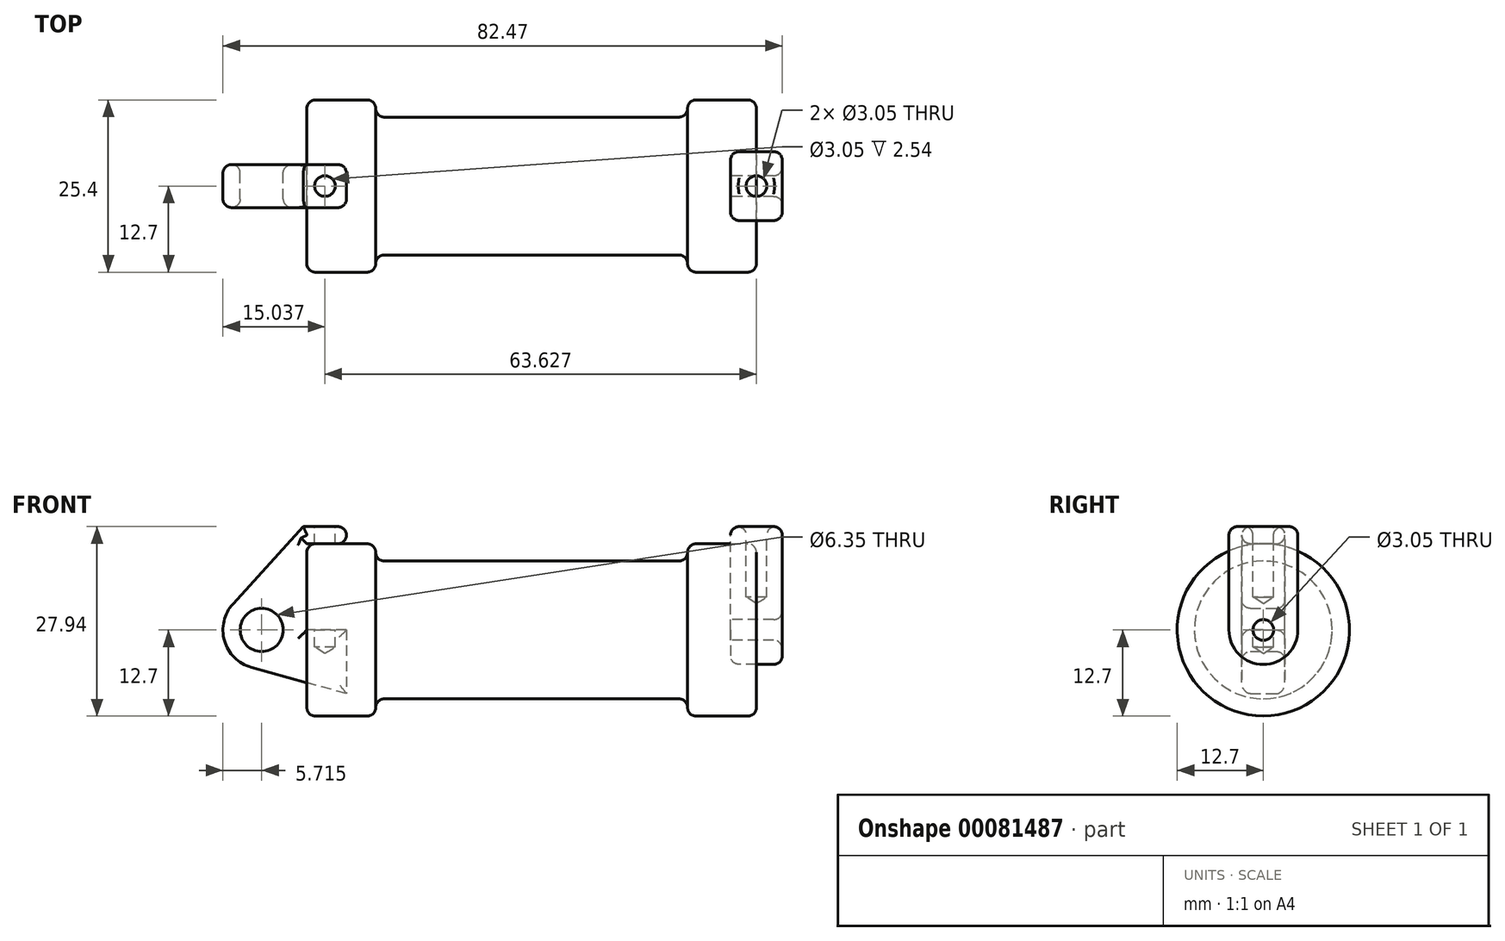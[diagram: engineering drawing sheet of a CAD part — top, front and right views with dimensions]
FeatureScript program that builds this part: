
annotation { "Feature Type Name" : "Feature", "Feature Type Description" : "" }
export const myFeature = defineFeature(function(context is Context, id is Id, definition is map)
    precondition{}
    {
        {
            var Q0;
            Q0=qCreatedBy(makeId("Front.planeOp"),FACE);
            var sketch = newSketch(context, id + "F0", { "sketchPlane" : qUnion([Q0])});
            skLineSegment(sketch, "E0", {"start": v(0, 0) * mm, "end": v(0, 12.7) * mm});
            skLineSegment(sketch, "E1", {"start": v(0, 12.7) * mm, "end": v(10.16, 12.7) * mm});
            skLineSegment(sketch, "E2", {"start": v(10.16, 12.7) * mm, "end": v(10.16, 10.16) * mm});
            skLineSegment(sketch, "E3", {"start": v(10.16, 10.16) * mm, "end": v(56.13, 10.16) * mm});
            skLineSegment(sketch, "E4", {"start": v(56.13, 10.16) * mm, "end": v(56.13, 12.7) * mm});
            skLineSegment(sketch, "E5", {"start": v(56.13, 12.7) * mm, "end": v(66.3, 12.7) * mm});
            skLineSegment(sketch, "E6", {"start": v(66.3, 12.7) * mm, "end": v(66.3, 0) * mm});
            skLineSegment(sketch, "E7", {"start": v(66.3, 0) * mm, "end": v(0, 0) * mm});
            skLineSegment(sketch, "E8", {"start": v(5.84, 15.24) * mm, "end": v(-0.5, 15.24) * mm});
            skLineSegment(sketch, "E9", {"start": v(-0.5, 15.24) * mm, "end": v(-10.88, 3.85) * mm});
            skLineSegment(sketch, "E10", {"start": v(0, 0) * mm, "end": v(-6.65, 0) * mm});
            skCircle(sketch, "E11", {"center": v(-6.65, 0) * mm, "radius": 5.72 * mm});
            skCircle(sketch, "E12", {"center": v(-6.65, 0) * mm, "radius": 3.18 * mm});
            skLineSegment(sketch, "E13", {"start": v(5.84, 15.24) * mm, "end": v(5.84, -9.4) * mm});
            skLineSegment(sketch, "E14", {"start": v(5.84, -9.4) * mm, "end": v(-8.18, -5.5) * mm});
            skSolve(sketch);
        }
        {
            var Q0;
            {var subQ0=sQuery(id+"F0.wireOp",EDGE,"E2");Q0=makeQuery(id+"F0.imprint","IMPRINT",FACE,{"disambiguationData":[TD([[makeQuery(id+"F0.imprint","IMPRINT",EDGE,{"derivedFrom":subQ0}),-1.0]])]});}
            var Q1;
            {var subQ0=sQuery(id+"F0.wireOp",EDGE,"E0");Q1=makeQuery(id+"F0.imprint","IMPRINT",FACE,{"disambiguationData":[TD([[makeQuery(id+"F0.imprint","IMPRINT",EDGE,{"derivedFrom":subQ0}),-1.0]])]});}
            var Q2;
            Q2=sQuery(id+"F0.wireOp",EDGE,"E7");
            revolve(context, id + "F1", {"entities" : qUnion([Q0, Q1]), "axis" : qUnion([Q2]), "revolveType" : RevolveType.FULL});
        }
        {
            var Q0;
            {var subQ3=sQuery(id+"F0.wireOp",EDGE,"E0");Q0=makeQuery(id+"F0.imprint","IMPRINT",FACE,{"disambiguationData":[TD([[makeQuery(id+"F0.imprint","IMPRINT",EDGE,{"derivedFrom":subQ3}),1.0]])]});}
            var Q1;
            {var subQ4=sQuery(id+"F0.wireOp",EDGE,"E12");Q1=makeQuery(id+"F0.imprint","IMPRINT",FACE,{"disambiguationData":[TD([[makeQuery(id+"F0.imprint","IMPRINT",EDGE,{"derivedFrom":subQ4}),-1.0]])]});}
            var Q2;
            {var subQ0=sQuery(id+"F0.wireOp",EDGE,"E14");Q2=makeQuery(id+"F0.imprint","IMPRINT",FACE,{"disambiguationData":[TD([[makeQuery(id+"F0.imprint","IMPRINT",EDGE,{"derivedFrom":subQ0}),-1.0]])]});}
            extrude(context, id + "F2", {"entities" : qUnion([Q0, Q1, Q2]), "endBound" : BoundingType.SYMMETRIC, "depth" : 6.35 * mm});
        }
        {
            var Q0;
            Q0=makeQuery(id+"F1.opRevolve","SWEPT_FACE",FACE,{"disambiguationData":[OSD([sQuery(id+"F0.wireOp",EDGE,"E6")])]});
            var sketch = newSketch(context, id + "F3", { "sketchPlane" : qUnion([Q0])});
            skCircle(sketch, "E15", {"center": v(0, 0) * mm, "radius": 5.08 * mm});
            skCircle(sketch, "E16", {"center": v(0, 0) * mm, "radius": 1.52 * mm});
            skLineSegment(sketch, "E17", {"start": v(-5.08, 0) * mm, "end": v(-5.08, 15.24) * mm});
            skLineSegment(sketch, "E18", {"start": v(5.08, 0) * mm, "end": v(5.08, 15.24) * mm});
            skLineSegment(sketch, "E19", {"start": v(-5.08, 15.24) * mm, "end": v(5.08, 15.24) * mm});
            skSolve(sketch);
        }
        {
            var Q0;
            {var subQ0=sQuery(id+"F3.wireOp",EDGE,"E17");var subQ1=sQuery(id+"F3.wireOp",EDGE,"E15");var subQ2=makeQuery(id+"F3.imprint","INTERSECT",VERTEX,{"derivedFrom":[subQ1,subQ0]});Q0=makeQuery(id+"F3.imprint","IMPRINT",FACE,{"disambiguationData":[TD([[makeQuery(id+"F3.imprint","IMPRINT",EDGE,{"disambiguationData":[TD([[subQ2,1.0]])],"derivedFrom":subQ1}),-1.0]])]});}
            var Q1;
            {var subQ0=sQuery(id+"F3.wireOp",EDGE,"E19");Q1=makeQuery(id+"F3.imprint","IMPRINT",FACE,{"disambiguationData":[TD([[makeQuery(id+"F3.imprint","IMPRINT",EDGE,{"derivedFrom":subQ0}),-1.0]])]});}
            var Q2;
            Q2=makeQuery(id+"F3.imprint","IMPRINT",FACE,{"disambiguationData":[TD([[makeQuery(id+"F3.imprint","IMPRINT",EDGE,{"derivedFrom":sQuery(id+"F3.wireOp",EDGE,"E16")}),-1.0]])]});
            extrude(context, id + "F4", {"entities" : qUnion([Q0, Q1, Q2]), "endBound" : BoundingType.SYMMETRIC, "depth" : 7.62 * mm});
        }
        {
            var Q0;
            Q0=makeQuery(id+"F2.opExtrude","SWEPT_FACE",FACE,{"disambiguationData":[OSD([sQuery(id+"F0.wireOp",EDGE,"E8")])]});
            var sketch = newSketch(context, id + "F5", { "sketchPlane" : qUnion([Q0])});
            skCircle(sketch, "E20", {"center": v(2.67, 0) * mm, "radius": 1.52 * mm});
            skSolve(sketch);
        }
        {
            var Q0;
            Q0=makeQuery(id+"F4.opExtrude","SWEPT_FACE",FACE,{"disambiguationData":[OSD([sQuery(id+"F3.wireOp",EDGE,"E19")])]});
            var sketch = newSketch(context, id + "F6", { "sketchPlane" : qUnion([Q0])});
            skCircle(sketch, "E21", {"center": v(66.3, 0) * mm, "radius": 1.52 * mm});
            skSolve(sketch);
        }
        {
            var Q0;
            Q0=sQuery(id+"F5.wireOp",VERTEX,"E20.center");
            var Q1;
            Q1=makeQuery(id+"F2.opExtrude","SWEPT_BODY",BODY,{"disambiguationData":[OSD([sQuery(id+"F0.wireOp",EDGE,"E0"),sQuery(id+"F0.wireOp",EDGE,"E1"),sQuery(id+"F0.wireOp",EDGE,"E7"),sQuery(id+"F0.wireOp",EDGE,"E8"),sQuery(id+"F0.wireOp",EDGE,"E9"),sQuery(id+"F0.wireOp",EDGE,"E11"),sQuery(id+"F0.wireOp",EDGE,"E12"),sQuery(id+"F0.wireOp",EDGE,"E13"),sQuery(id+"F0.wireOp",EDGE,"E14")])]});
            hole(context, id + "F7", {"style" : HoleStyle.SIMPLE, "endStyle" : HoleEndStyle.BLIND, "holeDiameter" : 3.05 * mm, "holeDepth" : 17.78 * mm, "locations" : qUnion([Q0]), "scope" : qUnion([Q1])});
        }
        {
            var Q0;
            Q0=sQuery(id+"F6.wireOp",VERTEX,"E21.center");
            var Q1;
            Q1=makeQuery(id+"F4.opExtrude","SWEPT_BODY",BODY,{"disambiguationData":[OSD([sQuery(id+"F3.wireOp",EDGE,"E15"),sQuery(id+"F3.wireOp",EDGE,"E16"),sQuery(id+"F3.wireOp",EDGE,"E17"),sQuery(id+"F3.wireOp",EDGE,"E18"),sQuery(id+"F3.wireOp",EDGE,"E19")])]});
            hole(context, id + "F8", {"style" : HoleStyle.SIMPLE, "endStyle" : HoleEndStyle.BLIND, "holeDiameter" : 3.05 * mm, "holeDepth" : 10.4 * mm, "locations" : qUnion([Q0]), "scope" : qUnion([Q1])});
        }
        {
            var Q0;
            Q0=makeQuery(id+"F1.opRevolve","SWEPT_EDGE",EDGE,{"disambiguationData":[OSD([sQuery(id+"F0.wireOp",EDGE,"E1"),sQuery(id+"F0.wireOp",EDGE,"E2")])]});
            var Q1;
            Q1=makeQuery(id+"F1.opRevolve","SWEPT_EDGE",EDGE,{"disambiguationData":[OSD([sQuery(id+"F0.wireOp",EDGE,"E2"),sQuery(id+"F0.wireOp",EDGE,"E3")])]});
            var Q2;
            Q2=makeQuery(id+"F1.opRevolve","SWEPT_EDGE",EDGE,{"disambiguationData":[OSD([sQuery(id+"F0.wireOp",EDGE,"E4"),sQuery(id+"F0.wireOp",EDGE,"E5")])]});
            var Q3;
            Q3=makeQuery(id+"F1.opRevolve","SWEPT_EDGE",EDGE,{"disambiguationData":[OSD([sQuery(id+"F0.wireOp",EDGE,"E3"),sQuery(id+"F0.wireOp",EDGE,"E4")])]});
            var Q4;
            Q4=makeQuery(id+"F1.opRevolve","SWEPT_FACE",FACE,{"disambiguationData":[OSD([sQuery(id+"F0.wireOp",EDGE,"E4")])]});
            var Q5;
            Q5=makeQuery(id+"F1.opRevolve","SWEPT_FACE",FACE,{"disambiguationData":[OSD([sQuery(id+"F0.wireOp",EDGE,"E3")])]});
            var Q6;
            Q6=makeQuery(id+"F1.opRevolve","SWEPT_EDGE",EDGE,{"disambiguationData":[OSD([sQuery(id+"F0.wireOp",EDGE,"E5"),sQuery(id+"F0.wireOp",EDGE,"E6")])]});
            var Q7;
            Q7=makeQuery(id+"F1.opRevolve","SWEPT_EDGE",EDGE,{"disambiguationData":[OSD([sQuery(id+"F0.wireOp",EDGE,"E0"),sQuery(id+"F0.wireOp",EDGE,"E1")])]});
            fillet(context, id + "F9", {"entities" : qUnion([Q0, Q1, Q2, Q3, Q4, Q5, Q6, Q7]), "radius" : 1.27 * mm, "tangentPropagation" : true, "allowEdgeOverflow" : false});
        }
        {
            var Q0;
            {var subQ0=sQuery(id+"F0.wireOp",EDGE,"E13");Q0=makeQuery(id+"F2.opExtrude","CAP_EDGE",EDGE,{"disambiguationData":[OSD([subQ0]),TDD([makeQuery(id+"F0.imprint","IMPRINT",EDGE,{"disambiguationData":[TD([[makeQuery(id+"F0.imprint","INTERSECT",VERTEX,{"derivedFrom":[sQuery(id+"F0.wireOp",EDGE,"E8"),subQ0]}),-1.0]])],"derivedFrom":subQ0})])],"isStart":false});}
            var Q1;
            Q1=makeQuery(id+"F2.opExtrude","SWEPT_EDGE",EDGE,{"disambiguationData":[OSD([sQuery(id+"F0.wireOp",EDGE,"E8"),sQuery(id+"F0.wireOp",EDGE,"E13")])]});
            var Q2;
            {var subQ0=sQuery(id+"F0.wireOp",EDGE,"E13");Q2=makeQuery(id+"F2.opExtrude","CAP_EDGE",EDGE,{"disambiguationData":[OSD([subQ0]),TDD([makeQuery(id+"F0.imprint","IMPRINT",EDGE,{"disambiguationData":[TD([[makeQuery(id+"F0.imprint","INTERSECT",VERTEX,{"derivedFrom":[sQuery(id+"F0.wireOp",EDGE,"E8"),subQ0]}),-1.0]])],"derivedFrom":subQ0})])],"isStart":true});}
            var Q3;
            Q3=makeQuery(id+"F2.opExtrude","SWEPT_EDGE",EDGE,{"disambiguationData":[OSD([sQuery(id+"F0.wireOp",EDGE,"E1"),sQuery(id+"F0.wireOp",EDGE,"E13")])]});
            var Q4;
            Q4=makeQuery(id+"F2.opExtrude","CAP_FACE",FACE,{"disambiguationData":[OSD([sQuery(id+"F0.wireOp",EDGE,"E0"),sQuery(id+"F0.wireOp",EDGE,"E1"),sQuery(id+"F0.wireOp",EDGE,"E7"),sQuery(id+"F0.wireOp",EDGE,"E8"),sQuery(id+"F0.wireOp",EDGE,"E9"),sQuery(id+"F0.wireOp",EDGE,"E11"),sQuery(id+"F0.wireOp",EDGE,"E12"),sQuery(id+"F0.wireOp",EDGE,"E13"),sQuery(id+"F0.wireOp",EDGE,"E14")])],"isStart":false});
            var Q5;
            Q5=makeQuery(id+"F2.opExtrude","CAP_FACE",FACE,{"disambiguationData":[OSD([sQuery(id+"F0.wireOp",EDGE,"E0"),sQuery(id+"F0.wireOp",EDGE,"E1"),sQuery(id+"F0.wireOp",EDGE,"E7"),sQuery(id+"F0.wireOp",EDGE,"E8"),sQuery(id+"F0.wireOp",EDGE,"E9"),sQuery(id+"F0.wireOp",EDGE,"E11"),sQuery(id+"F0.wireOp",EDGE,"E12"),sQuery(id+"F0.wireOp",EDGE,"E13"),sQuery(id+"F0.wireOp",EDGE,"E14")])],"isStart":true});
            var Q6;
            Q6=makeQuery(id+"F4.opExtrude","SWEPT_FACE",FACE,{"disambiguationData":[OSD([sQuery(id+"F3.wireOp",EDGE,"E18")])]});
            var Q7;
            Q7=makeQuery(id+"F4.opExtrude","SWEPT_FACE",FACE,{"disambiguationData":[OSD([sQuery(id+"F3.wireOp",EDGE,"E15")])]});
            var Q8;
            Q8=makeQuery(id+"F4.opExtrude","SWEPT_FACE",FACE,{"disambiguationData":[OSD([sQuery(id+"F3.wireOp",EDGE,"E19")])]});
            var Q9;
            Q9=makeQuery(id+"F4.opExtrude","CAP_FACE",FACE,{"disambiguationData":[OSD([sQuery(id+"F3.wireOp",EDGE,"E15"),sQuery(id+"F3.wireOp",EDGE,"E16"),sQuery(id+"F3.wireOp",EDGE,"E17"),sQuery(id+"F3.wireOp",EDGE,"E18"),sQuery(id+"F3.wireOp",EDGE,"E19")])],"isStart":false});
            fillet(context, id + "F10", {"entities" : qUnion([Q0, Q1, Q2, Q3, Q4, Q5, Q6, Q7, Q8, Q9]), "radius" : 1.27 * mm, "tangentPropagation" : true, "allowEdgeOverflow" : false});
        }
        {
            var Q0;
            Q0=makeQuery(id+"F1.opRevolve","SWEPT_FACE",FACE,{"disambiguationData":[OSD([sQuery(id+"F0.wireOp",EDGE,"E6")])]});
            var Q1;
            Q1=makeQuery(id+"F4.opExtrude","SWEPT_FACE",FACE,{"disambiguationData":[OSD([sQuery(id+"F3.wireOp",EDGE,"E18")])]});
            var Q2;
            {var subQ0=sQuery(id+"F3.wireOp",EDGE,"E18");Q2=makeQuery(id+"F10.opFillet","BLEND_EDGE",EDGE,{"blendedFrom":[makeQuery(id+"F4.opExtrude","CAP_EDGE",EDGE,{"disambiguationData":[OSD([subQ0])],"isStart":true}),makeQuery(id+"F4.opExtrude","SWEPT_FACE",FACE,{"disambiguationData":[OSD([subQ0])]})],"blendedInto":[makeQuery(id+"F4.opExtrude","SWEPT_FACE",FACE,{"disambiguationData":[OSD([subQ0])]})]});}
            var Q3;
            {var subQ0=sQuery(id+"F3.wireOp",EDGE,"E18");Q3=makeQuery(id+"F10.opFillet","BLEND_FACE",FACE,{"disambiguationData":[OSD([subQ0]),TDD([makeQuery(id+"F4.opExtrude","CAP_EDGE",EDGE,{"disambiguationData":[OSD([subQ0])],"isStart":false})])]});}
            var Q4;
            Q4=makeQuery(id+"F4.opExtrude","CAP_FACE",FACE,{"disambiguationData":[OSD([sQuery(id+"F3.wireOp",EDGE,"E15"),sQuery(id+"F3.wireOp",EDGE,"E16"),sQuery(id+"F3.wireOp",EDGE,"E17"),sQuery(id+"F3.wireOp",EDGE,"E18"),sQuery(id+"F3.wireOp",EDGE,"E19")])],"isStart":false});
            var Q5;
            {var subQ0=sQuery(id+"F3.wireOp",EDGE,"E17");Q5=makeQuery(id+"F10.opFillet","BLEND_EDGE",EDGE,{"blendedFrom":[makeQuery(id+"F4.opExtrude","CAP_EDGE",EDGE,{"disambiguationData":[OSD([subQ0])],"isStart":false}),makeQuery(id+"F4.opExtrude","SWEPT_FACE",FACE,{"disambiguationData":[OSD([subQ0])]})],"blendedInto":[makeQuery(id+"F4.opExtrude","SWEPT_FACE",FACE,{"disambiguationData":[OSD([subQ0])]})]});}
            var Q6;
            {var subQ0=sQuery(id+"F3.wireOp",EDGE,"E17");Q6=makeQuery(id+"F10.opFillet","BLEND_FACE",FACE,{"disambiguationData":[OSD([subQ0]),TDD([makeQuery(id+"F4.opExtrude","CAP_EDGE",EDGE,{"disambiguationData":[OSD([subQ0])],"isStart":false})])]});}
            var Q7;
            Q7=makeQuery(id+"F4.opExtrude","SWEPT_FACE",FACE,{"disambiguationData":[OSD([sQuery(id+"F3.wireOp",EDGE,"E17")])]});
            var Q8;
            Q8=makeQuery(id+"F4.opExtrude","CAP_FACE",FACE,{"disambiguationData":[OSD([sQuery(id+"F3.wireOp",EDGE,"E15"),sQuery(id+"F3.wireOp",EDGE,"E16"),sQuery(id+"F3.wireOp",EDGE,"E17"),sQuery(id+"F3.wireOp",EDGE,"E18"),sQuery(id+"F3.wireOp",EDGE,"E19")])],"isStart":true});
            var Q9;
            {var subQ0=sQuery(id+"F3.wireOp",EDGE,"E19");Q9=makeQuery(id+"F10.opFillet","BLEND_EDGE",EDGE,{"blendedFrom":[makeQuery(id+"F4.opExtrude","CAP_VERTEX",VERTEX,{"disambiguationData":[OSD([sQuery(id+"F3.wireOp",EDGE,"E18"),subQ0])],"isStart":true}),makeQuery(id+"F4.opExtrude","CAP_EDGE",EDGE,{"disambiguationData":[OSD([subQ0])],"isStart":true})],"blendedInto":[]});}
            var Q10;
            {var subQ0=sQuery(id+"F3.wireOp",EDGE,"E18");Q10=makeQuery(id+"F10.opFillet","BLEND_EDGE",EDGE,{"blendedFrom":[makeQuery(id+"F4.opExtrude","CAP_VERTEX",VERTEX,{"disambiguationData":[OSD([subQ0,sQuery(id+"F3.wireOp",EDGE,"E19")])],"isStart":true}),makeQuery(id+"F4.opExtrude","CAP_EDGE",EDGE,{"disambiguationData":[OSD([subQ0])],"isStart":true})],"blendedInto":[]});}
            var Q11;
            {var subQ0=sQuery(id+"F3.wireOp",EDGE,"E19");var subQ1=sQuery(id+"F3.wireOp",EDGE,"E18");Q11=makeQuery(id+"F10.opFillet","BLEND_EDGE",EDGE,{"blendedFrom":[makeQuery(id+"F4.opExtrude","CAP_VERTEX",VERTEX,{"disambiguationData":[OSD([subQ1,subQ0])],"isStart":true}),makeQuery(id+"F4.opExtrude","SWEPT_EDGE",EDGE,{"disambiguationData":[OSD([subQ1,subQ0])]})],"blendedInto":[]});}
            var Q12;
            {var subQ0=sQuery(id+"F3.wireOp",EDGE,"E19");Q12=makeQuery(id+"F10.opFillet","BLEND_EDGE",EDGE,{"blendedFrom":[makeQuery(id+"F4.opExtrude","CAP_EDGE",EDGE,{"disambiguationData":[OSD([subQ0])],"isStart":true}),makeQuery(id+"F4.opExtrude","CAP_FACE",FACE,{"disambiguationData":[OSD([sQuery(id+"F3.wireOp",EDGE,"E15"),sQuery(id+"F3.wireOp",EDGE,"E16"),sQuery(id+"F3.wireOp",EDGE,"E17"),sQuery(id+"F3.wireOp",EDGE,"E18"),subQ0])],"isStart":true})],"blendedInto":[makeQuery(id+"F4.opExtrude","CAP_FACE",FACE,{"disambiguationData":[OSD([sQuery(id+"F3.wireOp",EDGE,"E15"),sQuery(id+"F3.wireOp",EDGE,"E16"),sQuery(id+"F3.wireOp",EDGE,"E17"),sQuery(id+"F3.wireOp",EDGE,"E18"),subQ0])],"isStart":true})]});}
            var Q13;
            {var subQ0=sQuery(id+"F3.wireOp",EDGE,"E19");Q13=makeQuery(id+"F10.opFillet","BLEND_FACE",FACE,{"disambiguationData":[OSD([subQ0]),TDD([makeQuery(id+"F4.opExtrude","CAP_EDGE",EDGE,{"disambiguationData":[OSD([subQ0])],"isStart":true})])]});}
            var Q14;
            {var subQ0=sQuery(id+"F3.wireOp",EDGE,"E19");var subQ1=sQuery(id+"F3.wireOp",EDGE,"E17");Q14=makeQuery(id+"F10.opFillet","BLEND_EDGE",EDGE,{"blendedFrom":[makeQuery(id+"F4.opExtrude","CAP_VERTEX",VERTEX,{"disambiguationData":[OSD([subQ1,subQ0])],"isStart":true}),makeQuery(id+"F4.opExtrude","SWEPT_EDGE",EDGE,{"disambiguationData":[OSD([subQ1,subQ0])]})],"blendedInto":[]});}
            var Q15;
            {var subQ0=sQuery(id+"F3.wireOp",EDGE,"E17");Q15=makeQuery(id+"F10.opFillet","BLEND_EDGE",EDGE,{"blendedFrom":[makeQuery(id+"F4.opExtrude","CAP_VERTEX",VERTEX,{"disambiguationData":[OSD([subQ0,sQuery(id+"F3.wireOp",EDGE,"E19")])],"isStart":true}),makeQuery(id+"F4.opExtrude","CAP_EDGE",EDGE,{"disambiguationData":[OSD([subQ0])],"isStart":true})],"blendedInto":[]});}
            var Q16;
            {var subQ0=sQuery(id+"F0.wireOp",EDGE,"E0");Q16=makeQuery(id+"F10.opFillet","BLEND_FACE",FACE,{"disambiguationData":[OSD([subQ0]),TDD([makeQuery(id+"F2.opExtrude","CAP_EDGE",EDGE,{"disambiguationData":[OSD([subQ0])],"isStart":false})])]});}
            var Q17;
            Q17=makeQuery(id+"F10.opFillet","BLEND_EDGE",EDGE,{"blendedFrom":[makeQuery(id+"F2.opExtrude","CAP_EDGE",EDGE,{"disambiguationData":[OSD([sQuery(id+"F0.wireOp",EDGE,"E0")])],"isStart":false}),makeQuery(id+"F2.opExtrude","CAP_EDGE",EDGE,{"disambiguationData":[OSD([sQuery(id+"F0.wireOp",EDGE,"E7")])],"isStart":false})],"blendedInto":[]});
            var Q18;
            {var subQ0=sQuery(id+"F0.wireOp",EDGE,"E8");var subQ1=sQuery(id+"F0.wireOp",EDGE,"E1");Q18=makeQuery(id+"F10.opFillet","BLEND_FACE",FACE,{"disambiguationData":[OSD([subQ1,subQ0]),TDD([makeQuery(id+"F2.opExtrude","CAP_EDGE",EDGE,{"disambiguationData":[OSD([subQ1])],"isStart":false}),makeQuery(id+"F2.opExtrude","CAP_EDGE",EDGE,{"disambiguationData":[OSD([subQ0])],"isStart":false})])]});}
            var Q19;
            Q19=makeQuery(id+"F2.opExtrude","CAP_FACE",FACE,{"disambiguationData":[OSD([sQuery(id+"F0.wireOp",EDGE,"E0"),sQuery(id+"F0.wireOp",EDGE,"E1"),sQuery(id+"F0.wireOp",EDGE,"E7"),sQuery(id+"F0.wireOp",EDGE,"E8"),sQuery(id+"F0.wireOp",EDGE,"E9"),sQuery(id+"F0.wireOp",EDGE,"E11"),sQuery(id+"F0.wireOp",EDGE,"E12"),sQuery(id+"F0.wireOp",EDGE,"E13"),sQuery(id+"F0.wireOp",EDGE,"E14")])],"isStart":false});
            var Q20;
            {var subQ0=sQuery(id+"F0.wireOp",EDGE,"E14");Q20=makeQuery(id+"F10.opFillet","BLEND_EDGE",EDGE,{"blendedFrom":[makeQuery(id+"F2.opExtrude","CAP_EDGE",EDGE,{"disambiguationData":[OSD([subQ0])],"isStart":false}),makeQuery(id+"F2.opExtrude","SWEPT_FACE",FACE,{"disambiguationData":[OSD([subQ0])]})],"blendedInto":[makeQuery(id+"F2.opExtrude","SWEPT_FACE",FACE,{"disambiguationData":[OSD([subQ0])]})]});}
            var Q21;
            {var subQ0=sQuery(id+"F0.wireOp",EDGE,"E14");Q21=makeQuery(id+"F10.opFillet","BLEND_EDGE",EDGE,{"blendedFrom":[makeQuery(id+"F2.opExtrude","CAP_EDGE",EDGE,{"disambiguationData":[OSD([subQ0])],"isStart":true}),makeQuery(id+"F2.opExtrude","SWEPT_FACE",FACE,{"disambiguationData":[OSD([subQ0])]})],"blendedInto":[makeQuery(id+"F2.opExtrude","SWEPT_FACE",FACE,{"disambiguationData":[OSD([subQ0])]})]});}
            var Q22;
            {var subQ0=sQuery(id+"F0.wireOp",EDGE,"E14");Q22=makeQuery(id+"F10.opFillet","BLEND_FACE",FACE,{"disambiguationData":[OSD([subQ0]),TDD([makeQuery(id+"F2.opExtrude","CAP_EDGE",EDGE,{"disambiguationData":[OSD([subQ0])],"isStart":false})])]});}
            var Q23;
            Q23=makeQuery(id+"F2.opExtrude","SWEPT_FACE",FACE,{"disambiguationData":[OSD([sQuery(id+"F0.wireOp",EDGE,"E14")])]});
            var Q24;
            {var subQ0=sQuery(id+"F0.wireOp",EDGE,"E14");Q24=makeQuery(id+"F10.opFillet","BLEND_EDGE",EDGE,{"blendedFrom":[makeQuery(id+"F2.opExtrude","CAP_EDGE",EDGE,{"disambiguationData":[OSD([subQ0])],"isStart":true}),makeQuery(id+"F2.opExtrude","CAP_FACE",FACE,{"disambiguationData":[OSD([sQuery(id+"F0.wireOp",EDGE,"E0"),sQuery(id+"F0.wireOp",EDGE,"E1"),sQuery(id+"F0.wireOp",EDGE,"E7"),sQuery(id+"F0.wireOp",EDGE,"E8"),sQuery(id+"F0.wireOp",EDGE,"E9"),sQuery(id+"F0.wireOp",EDGE,"E11"),sQuery(id+"F0.wireOp",EDGE,"E12"),sQuery(id+"F0.wireOp",EDGE,"E13"),subQ0])],"isStart":true})],"blendedInto":[makeQuery(id+"F2.opExtrude","CAP_FACE",FACE,{"disambiguationData":[OSD([sQuery(id+"F0.wireOp",EDGE,"E0"),sQuery(id+"F0.wireOp",EDGE,"E1"),sQuery(id+"F0.wireOp",EDGE,"E7"),sQuery(id+"F0.wireOp",EDGE,"E8"),sQuery(id+"F0.wireOp",EDGE,"E9"),sQuery(id+"F0.wireOp",EDGE,"E11"),sQuery(id+"F0.wireOp",EDGE,"E12"),sQuery(id+"F0.wireOp",EDGE,"E13"),subQ0])],"isStart":true})]});}
            var Q25;
            Q25=makeQuery(id+"F2.opExtrude","CAP_FACE",FACE,{"disambiguationData":[OSD([sQuery(id+"F0.wireOp",EDGE,"E0"),sQuery(id+"F0.wireOp",EDGE,"E1"),sQuery(id+"F0.wireOp",EDGE,"E7"),sQuery(id+"F0.wireOp",EDGE,"E8"),sQuery(id+"F0.wireOp",EDGE,"E9"),sQuery(id+"F0.wireOp",EDGE,"E11"),sQuery(id+"F0.wireOp",EDGE,"E12"),sQuery(id+"F0.wireOp",EDGE,"E13"),sQuery(id+"F0.wireOp",EDGE,"E14")])],"isStart":true});
            var Q26;
            {var subQ0=sQuery(id+"F0.wireOp",EDGE,"E0");Q26=makeQuery(id+"F10.opFillet","BLEND_EDGE",EDGE,{"blendedFrom":[makeQuery(id+"F2.opExtrude","CAP_EDGE",EDGE,{"disambiguationData":[OSD([subQ0])],"isStart":true}),makeQuery(id+"F2.opExtrude","CAP_FACE",FACE,{"disambiguationData":[OSD([subQ0,sQuery(id+"F0.wireOp",EDGE,"E1"),sQuery(id+"F0.wireOp",EDGE,"E7"),sQuery(id+"F0.wireOp",EDGE,"E8"),sQuery(id+"F0.wireOp",EDGE,"E9"),sQuery(id+"F0.wireOp",EDGE,"E11"),sQuery(id+"F0.wireOp",EDGE,"E12"),sQuery(id+"F0.wireOp",EDGE,"E13"),sQuery(id+"F0.wireOp",EDGE,"E14")])],"isStart":true})],"blendedInto":[makeQuery(id+"F2.opExtrude","CAP_FACE",FACE,{"disambiguationData":[OSD([subQ0,sQuery(id+"F0.wireOp",EDGE,"E1"),sQuery(id+"F0.wireOp",EDGE,"E7"),sQuery(id+"F0.wireOp",EDGE,"E8"),sQuery(id+"F0.wireOp",EDGE,"E9"),sQuery(id+"F0.wireOp",EDGE,"E11"),sQuery(id+"F0.wireOp",EDGE,"E12"),sQuery(id+"F0.wireOp",EDGE,"E13"),sQuery(id+"F0.wireOp",EDGE,"E14")])],"isStart":true})]});}
            var Q27;
            {var subQ0=sQuery(id+"F0.wireOp",EDGE,"E8");var subQ1=sQuery(id+"F0.wireOp",EDGE,"E1");Q27=makeQuery(id+"F10.opFillet","BLEND_FACE",FACE,{"disambiguationData":[OSD([subQ1,subQ0]),TDD([makeQuery(id+"F2.opExtrude","CAP_EDGE",EDGE,{"disambiguationData":[OSD([subQ1])],"isStart":true}),makeQuery(id+"F2.opExtrude","CAP_EDGE",EDGE,{"disambiguationData":[OSD([subQ0])],"isStart":true})])]});}
            fillet(context, id + "F11", {"entities" : qUnion([Q0, Q1, Q2, Q3, Q4, Q5, Q6, Q7, Q8, Q9, Q10, Q11, Q12, Q13, Q14, Q15, Q16, Q17, Q18, Q19, Q20, Q21, Q22, Q23, Q24, Q25, Q26, Q27]), "radius" : 1.27 * mm, "tangentPropagation" : true, "allowEdgeOverflow" : false});
        }
    });
